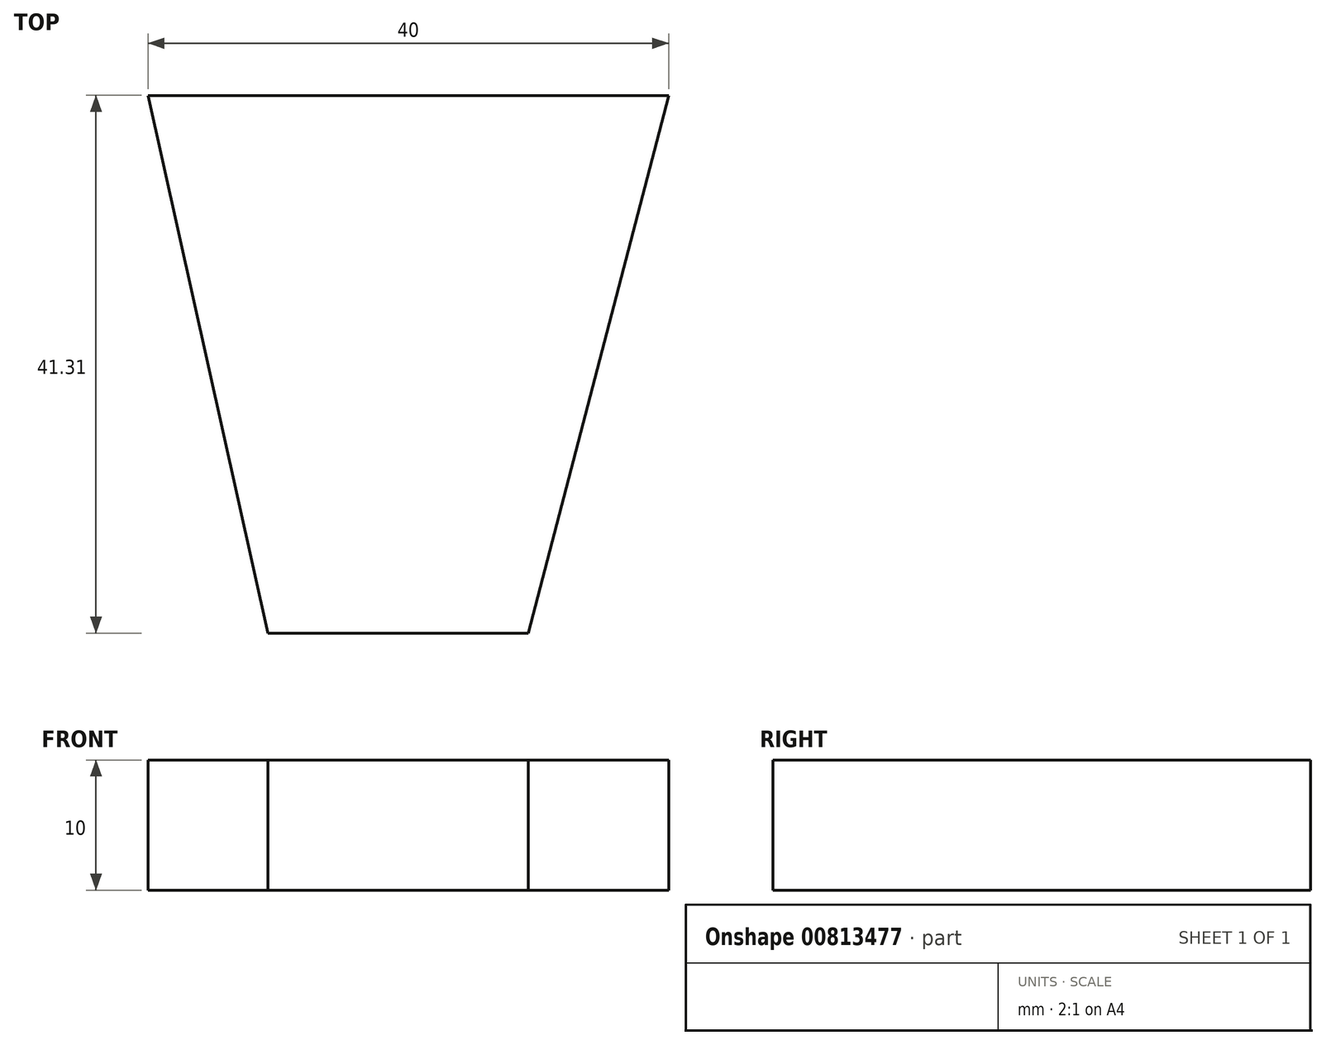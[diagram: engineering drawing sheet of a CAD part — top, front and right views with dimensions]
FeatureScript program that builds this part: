
annotation { "Feature Type Name" : "Feature", "Feature Type Description" : "" }
export const myFeature = defineFeature(function(context is Context, id is Id, definition is map)
    precondition{}
    {
        {
            var Q0;
            Q0=qCreatedBy(makeId("Top.planeOp"),FACE);
            var sketch = newSketch(context, id + "F0", { "sketchPlane" : qUnion([Q0])});
            skLineSegment(sketch, "E0", {"start": v(-29.2, 28.42) * mm, "end": v(10.8, 28.42) * mm});
            skLineSegment(sketch, "E1", {"start": v(-20, -12.89) * mm, "end": v(0, -12.89) * mm});
            skLineSegment(sketch, "E2", {"start": v(-29.2, 28.42) * mm, "end": v(-20, -12.89) * mm});
            skLineSegment(sketch, "E3", {"start": v(10.8, 28.42) * mm, "end": v(0, -12.89) * mm});
            skSolve(sketch);
        }
        {
            var Q0;
            Q0=makeQuery(id+"F0.imprint","IMPRINT",FACE,{"disambiguationData":[TD([[makeQuery(id+"F0.imprint","IMPRINT",EDGE,{"derivedFrom":sQuery(id+"F0.wireOp",EDGE,"E0")}),-1.0]])]});
            extrude(context, id + "F1", {"entities" : qUnion([Q0]), "depth" : 10 * mm, "offsetDistance" : 25 * mm});
        }
    });
